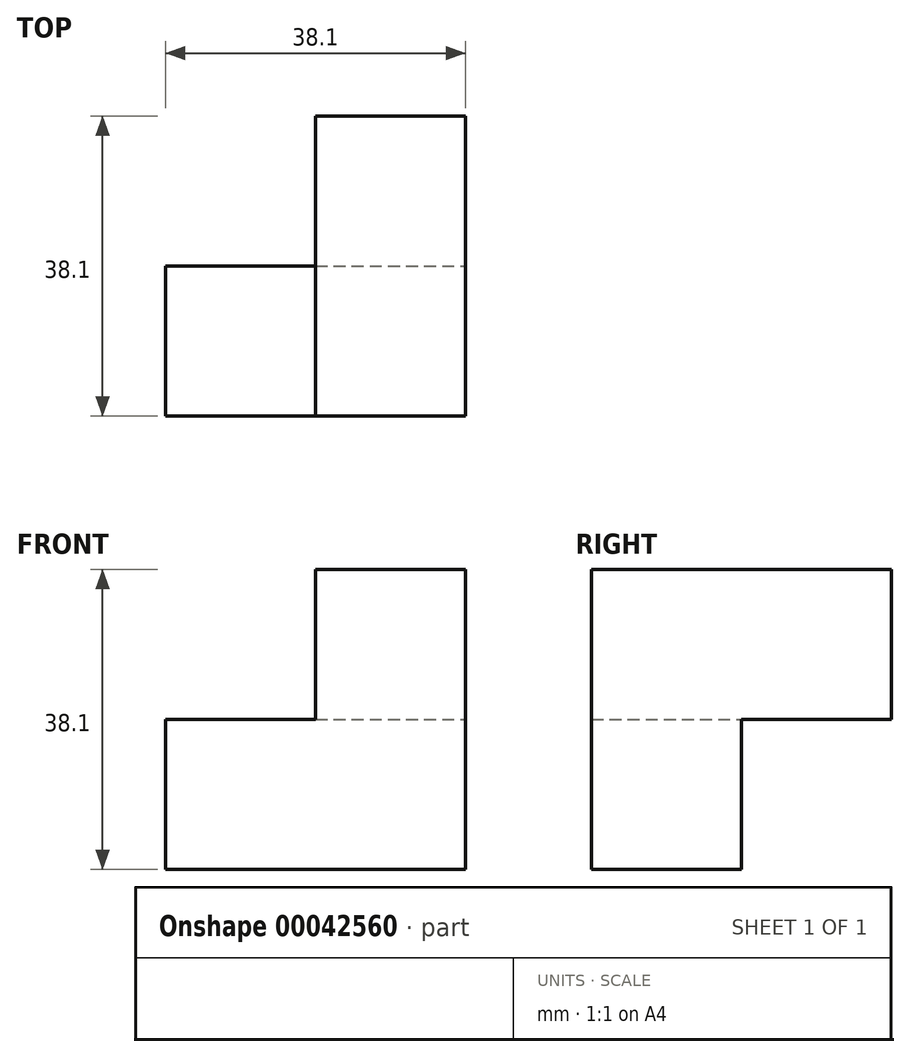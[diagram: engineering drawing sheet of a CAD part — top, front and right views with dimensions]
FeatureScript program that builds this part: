
annotation { "Feature Type Name" : "Feature", "Feature Type Description" : "" }
export const myFeature = defineFeature(function(context is Context, id is Id, definition is map)
    precondition{}
    {
        {
            var Q0;
            Q0=qCreatedBy(makeId("Right.planeOp"),FACE);
            var sketch = newSketch(context, id + "F0", { "sketchPlane" : qUnion([Q0])});
            skLineSegment(sketch, "E0.bottom", {"start": v(0, 0) * mm, "end": v(38.1, 0) * mm});
            skLineSegment(sketch, "E0.top", {"start": v(0, 38.1) * mm, "end": v(38.1, 38.1) * mm});
            skLineSegment(sketch, "E0.left", {"start": v(0, 0) * mm, "end": v(0, 38.1) * mm});
            skLineSegment(sketch, "E0.right", {"start": v(38.1, 0) * mm, "end": v(38.1, 38.1) * mm});
            skSolve(sketch);
        }
        {
            var Q0;
            Q0=qSketchRegion(id+"F0",true);
            extrude(context, id + "F1", {"entities" : qUnion([Q0]), "depth" : 19.05 * mm});
        }
        {
            var Q0;
            Q0=makeQuery(id+"F1.opExtrude","CAP_FACE",FACE,{"disambiguationData":[OSD([sQuery(id+"F0.wireOp",EDGE,"E0.bottom"),sQuery(id+"F0.wireOp",EDGE,"E0.top"),sQuery(id+"F0.wireOp",EDGE,"E0.left"),sQuery(id+"F0.wireOp",EDGE,"E0.right")])],"isStart":false});
            var sketch = newSketch(context, id + "F2", { "sketchPlane" : qUnion([Q0])});
            skLineSegment(sketch, "E1.bottom", {"start": v(38.1, 0) * mm, "end": v(19.05, 0) * mm});
            skLineSegment(sketch, "E1.top", {"start": v(38.1, 19.05) * mm, "end": v(19.05, 19.05) * mm});
            skLineSegment(sketch, "E1.left", {"start": v(38.1, 0) * mm, "end": v(38.1, 19.05) * mm});
            skLineSegment(sketch, "E1.right", {"start": v(19.05, 0) * mm, "end": v(19.05, 19.05) * mm});
            skSolve(sketch);
        }
        {
            var Q0;
            Q0=qSketchRegion(id+"F2",true);
            extrude(context, id + "F3", {"entities" : qUnion([Q0]), "operationType" : NewBodyOperationType.REMOVE, "oppositeDirection" : true, "depth" : 19.05 * mm});
        }
        {
            var Q0;
            Q0=makeQuery(id+"F1.opExtrude","CAP_FACE",FACE,{"disambiguationData":[OSD([sQuery(id+"F0.wireOp",EDGE,"E0.bottom"),sQuery(id+"F0.wireOp",EDGE,"E0.top"),sQuery(id+"F0.wireOp",EDGE,"E0.left"),sQuery(id+"F0.wireOp",EDGE,"E0.right")])],"isStart":true});
            var sketch = newSketch(context, id + "F4", { "sketchPlane" : qUnion([Q0])});
            skLineSegment(sketch, "E2.bottom", {"start": v(0, 0) * mm, "end": v(-19.05, 0) * mm});
            skLineSegment(sketch, "E2.top", {"start": v(0, 19.05) * mm, "end": v(-19.05, 19.05) * mm});
            skLineSegment(sketch, "E2.left", {"start": v(0, 0) * mm, "end": v(0, 19.05) * mm});
            skLineSegment(sketch, "E2.right", {"start": v(-19.05, 0) * mm, "end": v(-19.05, 19.05) * mm});
            skSolve(sketch);
        }
        {
            var Q0;
            Q0 = qSketchRegion(id + "F4", true);
            extrude(context, id + "F5", {"entities" : qUnion([Q0]), "operationType" : NewBodyOperationType.ADD, "depth" : 19.05 * mm});
        }
    });
